# Revit family: CLighting-Luminii-Vesta_2_GT
name_source: partatom
category: Lighting Fixtures
units: mm (PartAtom-declared; Revit-internal decimal feet)

## family parameters
Cut with Voids When Loaded = No
Host = Face
Light Source = Yes
OmniClass Number = 23.80.70.11.14.21
OmniClass Title = Spots and Tracklight Specialties
Part Type = Normal
Room Calculation Point = No
Round Connector Dimension = Use Diameter
Shared = Yes

## types (5) — shared parameters
Apparent Load = 4 VA
Assembly Code = D5020230
Color Filter = 16777215
Control Type = Consult Manufacturer Website for more Information
Control Zone = Consult Manufacturer Website for more Information
Current Amps = 50 A
Default Elevation = 0"
Depth = 3 9/16"
Description = Tegular T-grid linear
Dimming Lamp Color Temperature Shift = <None>
Dimming Type = Consult Manufacturer Website for more Information
Emit Shape Visible in Rendering = No
Emit from Rectangle Width = 2 3/8"
Environment = Indoor
Finish = Metal - Luminii - Silver Anodized Aluminum
Frequency = 60 Hz
Has Battery Backup = Yes
Has Dimming = Yes
Housing Protection Rating = Consult Manufacturer Website for more Information
Keynote = 26 50 00
Lamp Life = 1
Load Classification = Lighting
Luminaire Type = Recessed LED system designed for suspended tile ceilings
Manufacturer = Luminii
Model = Consult Manufacturer for More Information
Mounting Method = Designed for suspended tile ceilings
Number of Poles = 1
Operating Temperature = Consult Manufacturer Website for more Information
Phase = 1
Power Factor = 1
Power Source Type = Driver
Product Page URL = https://www.luminii.com
Tilt Angle = -90.00°
URL = https://www.luminii.com
Version = 2020 - v1.0a
Voltage = 120 V
Voltage Comments = 120/277/347V
Warranty URL = https://www.luminii.com
Wattage Comments = 3.8 W
Width = 3 7/16"

## per-type parameters (varying)
| type | C Length Mid | Constraints | Emit from Rectangle Length | Length | Photometric Web File |
| Vesta 2 GT - 4' | 24" | 2 | 48" | 48" | 363-90-4-35-F0-XX-04-00.ies |
| Vesta 2 GT - 6' | 36" | 4 | 72" | 72" | 364-90-4-35-F0-XX-06-00.ies |
| Vesta 2 GT - 8' | 48" | 5 | 96" | 96" | 363-90-4-35-F0-XX-08-00.ies |
| Vesta 2 GT - 10' | 60" | 6 | 120" | 120" | 363-90-4-35-F0-XX-10-00.ies |
| Vesta 2 GT - 12' | 72" | 7 | 144" | 144" | 363-90-4-35-F0-XX-12-00.ies |

## geometry (parser evidence)
native form markers: Sweep x13
no freeform markers — native parametric forms only
